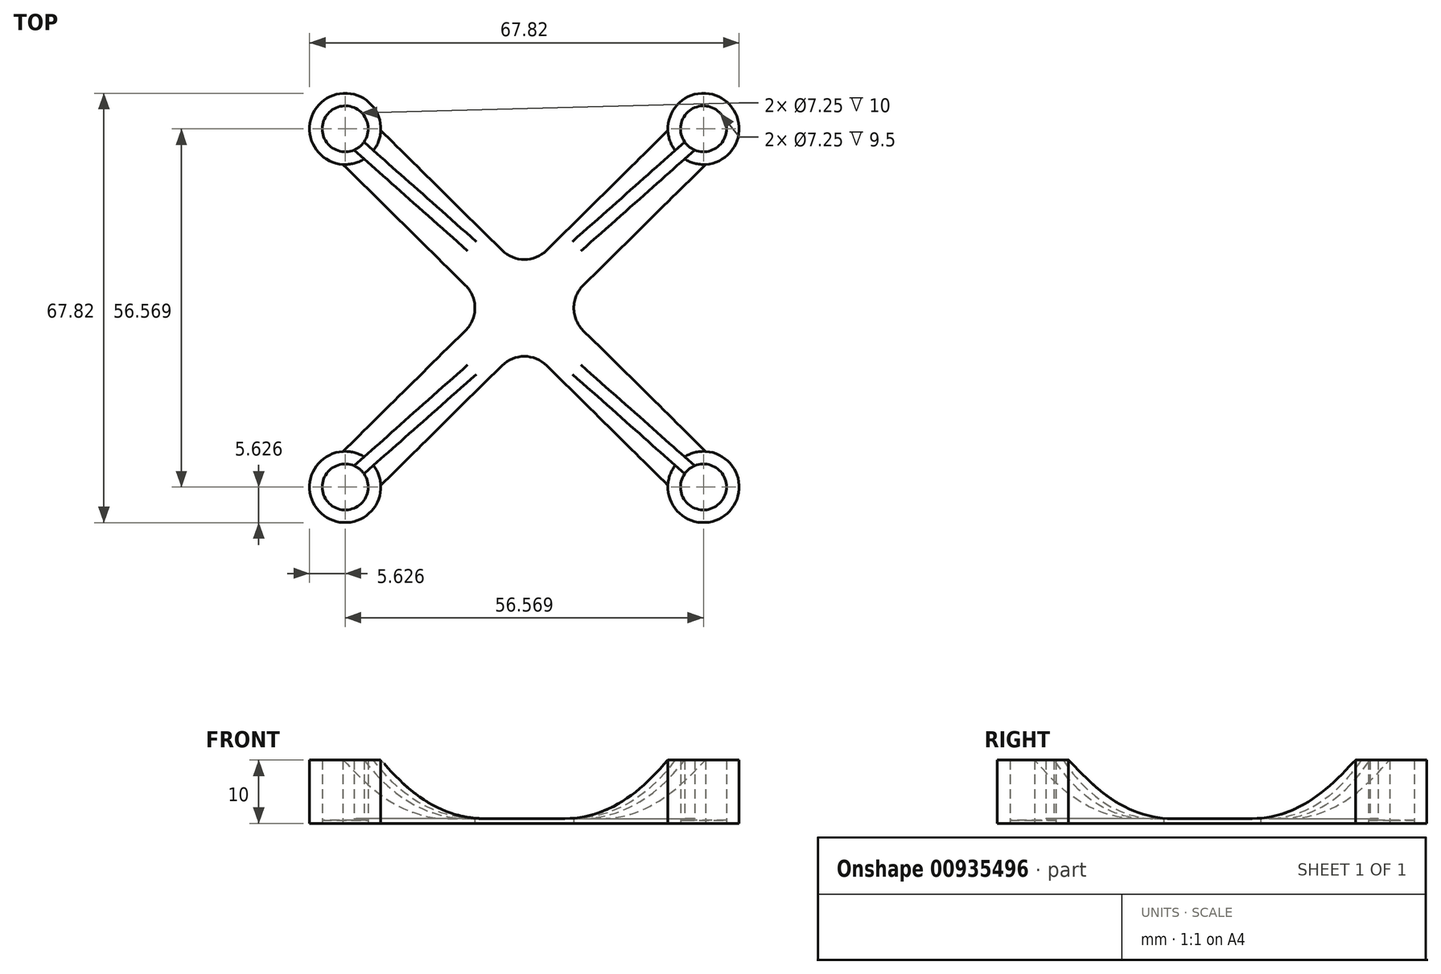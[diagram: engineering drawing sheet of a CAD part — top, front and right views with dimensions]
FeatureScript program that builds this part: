
annotation { "Feature Type Name" : "Feature", "Feature Type Description" : "" }
export const myFeature = defineFeature(function(context is Context, id is Id, definition is map)
    precondition{}
    {
        {
            var Q0;
            Q0=qCreatedBy(makeId("Top.planeOp"),FACE);
            var sketch = newSketch(context, id + "F0", { "sketchPlane" : qUnion([Q0])});
            skLineSegment(sketch, "E0", {"start": v(-28.63, 22.67) * mm, "end": v(22.67, -28.03) * mm});
            skLineSegment(sketch, "E1", {"start": v(28.63, -22.67) * mm, "end": v(-22.67, 28.03) * mm});
            skLineSegment(sketch, "E2.MirrorCS", {"start": v(28.63, 22.67) * mm, "end": v(-22.67, -28.03) * mm});
            skLineSegment(sketch, "E3.MirrorCS", {"start": v(-28.63, -22.67) * mm, "end": v(22.67, 28.03) * mm});
            skPoint(sketch, "E4", {"position": v(0, 5.62) * mm});
            skPoint(sketch, "E5", {"position": v(5.7, 0) * mm});
            skPoint(sketch, "E6", {"position": v(0, -5.62) * mm});
            skPoint(sketch, "E7", {"position": v(-5.7, 0) * mm});
            skPoint(sketch, "E8.middle", {"position": v(0, 0) * mm});
            skCircle(sketch, "E9.MirrorC", {"center": v(-28.28, 28.28) * mm, "radius": 3.62 * mm});
            skCircle(sketch, "E10", {"center": v(-28.28, 28.28) * mm, "radius": 5.62 * mm});
            skCircle(sketch, "E11.MirrorC", {"center": v(28.28, 28.28) * mm, "radius": 3.62 * mm});
            skCircle(sketch, "E12.MirrorC", {"center": v(28.28, 28.28) * mm, "radius": 5.62 * mm});
            skCircle(sketch, "E13.MirrorC", {"center": v(28.28, -28.28) * mm, "radius": 5.62 * mm});
            skCircle(sketch, "E14.MirrorC", {"center": v(28.28, -28.28) * mm, "radius": 3.62 * mm});
            skCircle(sketch, "E15.MirrorC", {"center": v(-28.28, -28.28) * mm, "radius": 5.62 * mm});
            skCircle(sketch, "E16.MirrorC", {"center": v(-28.28, -28.28) * mm, "radius": 3.62 * mm});
            skLineSegment(sketch, "E17", {"start": v(-28.28, 28.28) * mm, "end": v(-28.28, -28.28) * mm, "construction": true});
            skLineSegment(sketch, "E18", {"start": v(28.28, -28.28) * mm, "end": v(28.28, 28.28) * mm, "construction": true});
            skLineSegment(sketch, "E19", {"start": v(28.28, 28.28) * mm, "end": v(-28.28, 28.28) * mm, "construction": true});
            skLineSegment(sketch, "E20", {"start": v(-28.28, -28.28) * mm, "end": v(28.28, -28.28) * mm, "construction": true});
            skLineSegment(sketch, "E21", {"start": v(-25.31, 26.2) * mm, "end": v(-23.81, 24.87) * mm});
            skLineSegment(sketch, "E22", {"start": v(-26.9, 24.94) * mm, "end": v(-25.3, 23.52) * mm});
            skLineSegment(sketch, "E23.MirrorCS", {"start": v(26.9, 24.94) * mm, "end": v(25.3, 23.52) * mm});
            skLineSegment(sketch, "E24.MirrorCS", {"start": v(25.31, 26.2) * mm, "end": v(23.81, 24.87) * mm});
            skLineSegment(sketch, "E25.MirrorCS", {"start": v(26.9, -24.94) * mm, "end": v(25.3, -23.52) * mm});
            skLineSegment(sketch, "E26.MirrorCS", {"start": v(25.31, -26.2) * mm, "end": v(23.81, -24.87) * mm});
            skLineSegment(sketch, "E27.MirrorCS", {"start": v(-26.9, -24.94) * mm, "end": v(-25.3, -23.52) * mm});
            skLineSegment(sketch, "E28.MirrorCS", {"start": v(-25.31, -26.2) * mm, "end": v(-23.81, -24.87) * mm});
            skSolve(sketch);
        }
        {
            var Q0;
            {var subQ0=sQuery(id+"F0.wireOp",EDGE,"E3.MirrorCS");var subQ1=sQuery(id+"F0.wireOp",EDGE,"E0");var subQ2=makeQuery(id+"F0.imprint","INTERSECT",VERTEX,{"derivedFrom":[subQ1,subQ0]});Q0=makeQuery(id+"F0.imprint","IMPRINT",FACE,{"disambiguationData":[TD([[makeQuery(id+"F0.imprint","IMPRINT",EDGE,{"disambiguationData":[TD([[subQ2,-1.0]])],"derivedFrom":subQ1}),-1.0]])]});}
            var Q1;
            {var subQ0=sQuery(id+"F0.wireOp",EDGE,"E10");var subQ1=sQuery(id+"F0.wireOp",EDGE,"E0");var subQ2=makeQuery(id+"F0.imprint","INTERSECT",VERTEX,{"derivedFrom":[subQ1,subQ0]});Q1=makeQuery(id+"F0.imprint","IMPRINT",FACE,{"disambiguationData":[TD([[makeQuery(id+"F0.imprint","IMPRINT",EDGE,{"disambiguationData":[TD([[subQ2,-1.0]])],"derivedFrom":subQ1}),1.0]])]});}
            var Q2;
            {var subQ0=sQuery(id+"F0.wireOp",EDGE,"E2.MirrorCS");var subQ1=sQuery(id+"F0.wireOp",EDGE,"E1");var subQ2=makeQuery(id+"F0.imprint","INTERSECT",VERTEX,{"derivedFrom":[subQ1,subQ0]});Q2=makeQuery(id+"F0.imprint","IMPRINT",FACE,{"disambiguationData":[TD([[makeQuery(id+"F0.imprint","IMPRINT",EDGE,{"disambiguationData":[TD([[subQ2,-1.0]])],"derivedFrom":subQ1}),-1.0]])]});}
            var Q3;
            {var subQ0=sQuery(id+"F0.wireOp",EDGE,"E13.MirrorC");var subQ1=sQuery(id+"F0.wireOp",EDGE,"E0");var subQ2=makeQuery(id+"F0.imprint","INTERSECT",VERTEX,{"derivedFrom":[subQ1,subQ0]});Q3=makeQuery(id+"F0.imprint","IMPRINT",FACE,{"disambiguationData":[TD([[makeQuery(id+"F0.imprint","IMPRINT",EDGE,{"disambiguationData":[TD([[subQ2,1.0]])],"derivedFrom":subQ1}),1.0]])]});}
            var Q4;
            {var subQ0=sQuery(id+"F0.wireOp",EDGE,"E3.MirrorCS");var subQ1=sQuery(id+"F0.wireOp",EDGE,"E0");var subQ2=makeQuery(id+"F0.imprint","INTERSECT",VERTEX,{"derivedFrom":[subQ1,subQ0]});Q4=makeQuery(id+"F0.imprint","IMPRINT",FACE,{"disambiguationData":[TD([[makeQuery(id+"F0.imprint","IMPRINT",EDGE,{"disambiguationData":[TD([[subQ2,-1.0]])],"derivedFrom":subQ1}),1.0]])]});}
            var Q5;
            {var subQ3=sQuery(id+"F0.wireOp",EDGE,"E21");Q5=makeQuery(id+"F0.imprint","IMPRINT",FACE,{"disambiguationData":[TD([[makeQuery(id+"F0.imprint","IMPRINT",EDGE,{"derivedFrom":subQ3}),1.0]])]});}
            var Q6;
            {var subQ4=sQuery(id+"F0.wireOp",EDGE,"E23.MirrorCS");Q6=makeQuery(id+"F0.imprint","IMPRINT",FACE,{"disambiguationData":[TD([[makeQuery(id+"F0.imprint","IMPRINT",EDGE,{"derivedFrom":subQ4}),1.0]])]});}
            var Q7;
            {var subQ4=sQuery(id+"F0.wireOp",EDGE,"E25.MirrorCS");Q7=makeQuery(id+"F0.imprint","IMPRINT",FACE,{"disambiguationData":[TD([[makeQuery(id+"F0.imprint","IMPRINT",EDGE,{"derivedFrom":subQ4}),-1.0]])]});}
            var Q8;
            {var subQ4=sQuery(id+"F0.wireOp",EDGE,"E27.MirrorCS");Q8=makeQuery(id+"F0.imprint","IMPRINT",FACE,{"disambiguationData":[TD([[makeQuery(id+"F0.imprint","IMPRINT",EDGE,{"derivedFrom":subQ4}),1.0]])]});}
            var Q9;
            {var subQ0=sQuery(id+"F0.wireOp",EDGE,"E23.MirrorCS");Q9=makeQuery(id+"F0.imprint","IMPRINT",FACE,{"disambiguationData":[TD([[makeQuery(id+"F0.imprint","IMPRINT",EDGE,{"derivedFrom":subQ0}),-1.0]])]});}
            var Q10;
            {var subQ0=sQuery(id+"F0.wireOp",EDGE,"E21");Q10=makeQuery(id+"F0.imprint","IMPRINT",FACE,{"disambiguationData":[TD([[makeQuery(id+"F0.imprint","IMPRINT",EDGE,{"derivedFrom":subQ0}),-1.0]])]});}
            var Q11;
            {var subQ0=sQuery(id+"F0.wireOp",EDGE,"E27.MirrorCS");Q11=makeQuery(id+"F0.imprint","IMPRINT",FACE,{"disambiguationData":[TD([[makeQuery(id+"F0.imprint","IMPRINT",EDGE,{"derivedFrom":subQ0}),-1.0]])]});}
            var Q12;
            {var subQ0=sQuery(id+"F0.wireOp",EDGE,"E25.MirrorCS");Q12=makeQuery(id+"F0.imprint","IMPRINT",FACE,{"disambiguationData":[TD([[makeQuery(id+"F0.imprint","IMPRINT",EDGE,{"derivedFrom":subQ0}),1.0]])]});}
            extrude(context, id + "F1", {"entities" : qUnion([Q0, Q1, Q2, Q3, Q4, Q5, Q6, Q7, Q8, Q9, Q10, Q11, Q12]), "depth" : 0.75 * mm, "offsetDistance" : 25 * mm});
        }
        {
            var Q0;
            {var subQ4=sQuery(id+"F0.wireOp",EDGE,"E27.MirrorCS");Q0=makeQuery(id+"F0.imprint","IMPRINT",FACE,{"disambiguationData":[TD([[makeQuery(id+"F0.imprint","IMPRINT",EDGE,{"derivedFrom":subQ4}),1.0]])]});}
            var Q1;
            {var subQ4=sQuery(id+"F0.wireOp",EDGE,"E25.MirrorCS");Q1=makeQuery(id+"F0.imprint","IMPRINT",FACE,{"disambiguationData":[TD([[makeQuery(id+"F0.imprint","IMPRINT",EDGE,{"derivedFrom":subQ4}),-1.0]])]});}
            var Q2;
            {var subQ4=sQuery(id+"F0.wireOp",EDGE,"E23.MirrorCS");Q2=makeQuery(id+"F0.imprint","IMPRINT",FACE,{"disambiguationData":[TD([[makeQuery(id+"F0.imprint","IMPRINT",EDGE,{"derivedFrom":subQ4}),1.0]])]});}
            var Q3;
            {var subQ3=sQuery(id+"F0.wireOp",EDGE,"E21");Q3=makeQuery(id+"F0.imprint","IMPRINT",FACE,{"disambiguationData":[TD([[makeQuery(id+"F0.imprint","IMPRINT",EDGE,{"derivedFrom":subQ3}),1.0]])]});}
            extrude(context, id + "F2", {"entities" : qUnion([Q0, Q1, Q2, Q3]), "operationType" : NewBodyOperationType.ADD, "depth" : 10 * mm, "offsetDistance" : 25 * mm});
        }
        {
            var Q0;
            Q0=makeQuery(id+"F1.opExtrude","SWEPT_EDGE",EDGE,{"disambiguationData":[OSD([sQuery(id+"F0.wireOp",EDGE,"E1"),sQuery(id+"F0.wireOp",EDGE,"E2.MirrorCS")])]});
            var Q1;
            Q1=makeQuery(id+"F1.opExtrude","SWEPT_EDGE",EDGE,{"disambiguationData":[OSD([sQuery(id+"F0.wireOp",EDGE,"E1"),sQuery(id+"F0.wireOp",EDGE,"E3.MirrorCS")])]});
            var Q2;
            Q2=makeQuery(id+"F1.opExtrude","SWEPT_EDGE",EDGE,{"disambiguationData":[OSD([sQuery(id+"F0.wireOp",EDGE,"E0"),sQuery(id+"F0.wireOp",EDGE,"E3.MirrorCS")])]});
            var Q3;
            Q3=makeQuery(id+"F1.opExtrude","SWEPT_EDGE",EDGE,{"disambiguationData":[OSD([sQuery(id+"F0.wireOp",EDGE,"E0"),sQuery(id+"F0.wireOp",EDGE,"E2.MirrorCS")])]});
            fillet(context, id + "F3", {"entities" : qUnion([Q0, Q1, Q2, Q3]), "radius" : 5 * mm, "tangentPropagation" : true, "allowEdgeOverflow" : false});
        }
        {
            var Q0;
            Q0=makeQuery(id+"F0.imprint","IMPRINT",FACE,{"disambiguationData":[TD([[makeQuery(id+"F0.imprint","IMPRINT",EDGE,{"derivedFrom":sQuery(id+"F0.wireOp",EDGE,"E9.MirrorC")}),-1.0]])]});
            var Q1;
            Q1=makeQuery(id+"F0.imprint","IMPRINT",FACE,{"disambiguationData":[TD([[makeQuery(id+"F0.imprint","IMPRINT",EDGE,{"derivedFrom":sQuery(id+"F0.wireOp",EDGE,"E11.MirrorC")}),1.0]])]});
            var Q2;
            Q2=makeQuery(id+"F0.imprint","IMPRINT",FACE,{"disambiguationData":[TD([[makeQuery(id+"F0.imprint","IMPRINT",EDGE,{"derivedFrom":sQuery(id+"F0.wireOp",EDGE,"E14.MirrorC")}),-1.0]])]});
            var Q3;
            Q3=makeQuery(id+"F0.imprint","IMPRINT",FACE,{"disambiguationData":[TD([[makeQuery(id+"F0.imprint","IMPRINT",EDGE,{"derivedFrom":sQuery(id+"F0.wireOp",EDGE,"E16.MirrorC")}),1.0]])]});
            extrude(context, id + "F4", {"entities" : qUnion([Q0, Q1, Q2, Q3]), "operationType" : NewBodyOperationType.ADD, "depth" : .5 * mm, "offsetDistance" : 25 * mm});
        }
        {
            var Q0;
            {var subQ0=sQuery(id+"F0.wireOp",EDGE,"E10");Q0=makeQuery(id+"F2.boolean.opBoolean","INTERSECT",EDGE,{"disambiguationData":[OD(0.0)],"derivedFrom":[makeQuery(id+"F1.opExtrude","CAP_FACE",FACE,{"disambiguationData":[OSD([sQuery(id+"F0.wireOp",EDGE,"E0"),sQuery(id+"F0.wireOp",EDGE,"E1"),sQuery(id+"F0.wireOp",EDGE,"E2.MirrorCS"),sQuery(id+"F0.wireOp",EDGE,"E3.MirrorCS"),sQuery(id+"F0.wireOp",EDGE,"E9.MirrorC"),subQ0,sQuery(id+"F0.wireOp",EDGE,"E11.MirrorC"),sQuery(id+"F0.wireOp",EDGE,"E12.MirrorC"),sQuery(id+"F0.wireOp",EDGE,"E13.MirrorC"),sQuery(id+"F0.wireOp",EDGE,"E14.MirrorC"),sQuery(id+"F0.wireOp",EDGE,"E15.MirrorC"),sQuery(id+"F0.wireOp",EDGE,"E16.MirrorC")])],"isStart":false}),makeQuery(id+"F2.opExtrude","SWEPT_FACE",FACE,{"disambiguationData":[OSD([subQ0])]})]});}
            var Q1;
            {var subQ0=sQuery(id+"F0.wireOp",EDGE,"E10");Q1=makeQuery(id+"F2.boolean.opBoolean","INTERSECT",EDGE,{"disambiguationData":[OD(1.0)],"derivedFrom":[makeQuery(id+"F1.opExtrude","CAP_FACE",FACE,{"disambiguationData":[OSD([sQuery(id+"F0.wireOp",EDGE,"E0"),sQuery(id+"F0.wireOp",EDGE,"E1"),sQuery(id+"F0.wireOp",EDGE,"E2.MirrorCS"),sQuery(id+"F0.wireOp",EDGE,"E3.MirrorCS"),sQuery(id+"F0.wireOp",EDGE,"E9.MirrorC"),subQ0,sQuery(id+"F0.wireOp",EDGE,"E11.MirrorC"),sQuery(id+"F0.wireOp",EDGE,"E12.MirrorC"),sQuery(id+"F0.wireOp",EDGE,"E13.MirrorC"),sQuery(id+"F0.wireOp",EDGE,"E14.MirrorC"),sQuery(id+"F0.wireOp",EDGE,"E15.MirrorC"),sQuery(id+"F0.wireOp",EDGE,"E16.MirrorC")])],"isStart":false}),makeQuery(id+"F2.opExtrude","SWEPT_FACE",FACE,{"disambiguationData":[OSD([subQ0])]})]});}
            var Q2;
            {var subQ0=sQuery(id+"F0.wireOp",EDGE,"E15.MirrorC");Q2=makeQuery(id+"F2.boolean.opBoolean","INTERSECT",EDGE,{"disambiguationData":[OD(0.0)],"derivedFrom":[makeQuery(id+"F1.opExtrude","CAP_FACE",FACE,{"disambiguationData":[OSD([sQuery(id+"F0.wireOp",EDGE,"E0"),sQuery(id+"F0.wireOp",EDGE,"E1"),sQuery(id+"F0.wireOp",EDGE,"E2.MirrorCS"),sQuery(id+"F0.wireOp",EDGE,"E3.MirrorCS"),sQuery(id+"F0.wireOp",EDGE,"E9.MirrorC"),sQuery(id+"F0.wireOp",EDGE,"E10"),sQuery(id+"F0.wireOp",EDGE,"E11.MirrorC"),sQuery(id+"F0.wireOp",EDGE,"E12.MirrorC"),sQuery(id+"F0.wireOp",EDGE,"E13.MirrorC"),sQuery(id+"F0.wireOp",EDGE,"E14.MirrorC"),subQ0,sQuery(id+"F0.wireOp",EDGE,"E16.MirrorC")])],"isStart":false}),makeQuery(id+"F2.opExtrude","SWEPT_FACE",FACE,{"disambiguationData":[OSD([subQ0])]})]});}
            var Q3;
            {var subQ0=sQuery(id+"F0.wireOp",EDGE,"E15.MirrorC");Q3=makeQuery(id+"F2.boolean.opBoolean","INTERSECT",EDGE,{"disambiguationData":[OD(1.0)],"derivedFrom":[makeQuery(id+"F1.opExtrude","CAP_FACE",FACE,{"disambiguationData":[OSD([sQuery(id+"F0.wireOp",EDGE,"E0"),sQuery(id+"F0.wireOp",EDGE,"E1"),sQuery(id+"F0.wireOp",EDGE,"E2.MirrorCS"),sQuery(id+"F0.wireOp",EDGE,"E3.MirrorCS"),sQuery(id+"F0.wireOp",EDGE,"E9.MirrorC"),sQuery(id+"F0.wireOp",EDGE,"E10"),sQuery(id+"F0.wireOp",EDGE,"E11.MirrorC"),sQuery(id+"F0.wireOp",EDGE,"E12.MirrorC"),sQuery(id+"F0.wireOp",EDGE,"E13.MirrorC"),sQuery(id+"F0.wireOp",EDGE,"E14.MirrorC"),subQ0,sQuery(id+"F0.wireOp",EDGE,"E16.MirrorC")])],"isStart":false}),makeQuery(id+"F2.opExtrude","SWEPT_FACE",FACE,{"disambiguationData":[OSD([subQ0])]})]});}
            var Q4;
            {var subQ0=sQuery(id+"F0.wireOp",EDGE,"E12.MirrorC");Q4=makeQuery(id+"F2.boolean.opBoolean","INTERSECT",EDGE,{"disambiguationData":[OD(0.0)],"derivedFrom":[makeQuery(id+"F1.opExtrude","CAP_FACE",FACE,{"disambiguationData":[OSD([sQuery(id+"F0.wireOp",EDGE,"E0"),sQuery(id+"F0.wireOp",EDGE,"E1"),sQuery(id+"F0.wireOp",EDGE,"E2.MirrorCS"),sQuery(id+"F0.wireOp",EDGE,"E3.MirrorCS"),sQuery(id+"F0.wireOp",EDGE,"E9.MirrorC"),sQuery(id+"F0.wireOp",EDGE,"E10"),sQuery(id+"F0.wireOp",EDGE,"E11.MirrorC"),subQ0,sQuery(id+"F0.wireOp",EDGE,"E13.MirrorC"),sQuery(id+"F0.wireOp",EDGE,"E14.MirrorC"),sQuery(id+"F0.wireOp",EDGE,"E15.MirrorC"),sQuery(id+"F0.wireOp",EDGE,"E16.MirrorC")])],"isStart":false}),makeQuery(id+"F2.opExtrude","SWEPT_FACE",FACE,{"disambiguationData":[OSD([subQ0])]})]});}
            var Q5;
            {var subQ0=sQuery(id+"F0.wireOp",EDGE,"E12.MirrorC");Q5=makeQuery(id+"F2.boolean.opBoolean","INTERSECT",EDGE,{"disambiguationData":[OD(1.0)],"derivedFrom":[makeQuery(id+"F1.opExtrude","CAP_FACE",FACE,{"disambiguationData":[OSD([sQuery(id+"F0.wireOp",EDGE,"E0"),sQuery(id+"F0.wireOp",EDGE,"E1"),sQuery(id+"F0.wireOp",EDGE,"E2.MirrorCS"),sQuery(id+"F0.wireOp",EDGE,"E3.MirrorCS"),sQuery(id+"F0.wireOp",EDGE,"E9.MirrorC"),sQuery(id+"F0.wireOp",EDGE,"E10"),sQuery(id+"F0.wireOp",EDGE,"E11.MirrorC"),subQ0,sQuery(id+"F0.wireOp",EDGE,"E13.MirrorC"),sQuery(id+"F0.wireOp",EDGE,"E14.MirrorC"),sQuery(id+"F0.wireOp",EDGE,"E15.MirrorC"),sQuery(id+"F0.wireOp",EDGE,"E16.MirrorC")])],"isStart":false}),makeQuery(id+"F2.opExtrude","SWEPT_FACE",FACE,{"disambiguationData":[OSD([subQ0])]})]});}
            var Q6;
            {var subQ0=sQuery(id+"F0.wireOp",EDGE,"E13.MirrorC");Q6=makeQuery(id+"F2.boolean.opBoolean","INTERSECT",EDGE,{"disambiguationData":[OD(0.0)],"derivedFrom":[makeQuery(id+"F1.opExtrude","CAP_FACE",FACE,{"disambiguationData":[OSD([sQuery(id+"F0.wireOp",EDGE,"E0"),sQuery(id+"F0.wireOp",EDGE,"E1"),sQuery(id+"F0.wireOp",EDGE,"E2.MirrorCS"),sQuery(id+"F0.wireOp",EDGE,"E3.MirrorCS"),sQuery(id+"F0.wireOp",EDGE,"E9.MirrorC"),sQuery(id+"F0.wireOp",EDGE,"E10"),sQuery(id+"F0.wireOp",EDGE,"E11.MirrorC"),sQuery(id+"F0.wireOp",EDGE,"E12.MirrorC"),subQ0,sQuery(id+"F0.wireOp",EDGE,"E14.MirrorC"),sQuery(id+"F0.wireOp",EDGE,"E15.MirrorC"),sQuery(id+"F0.wireOp",EDGE,"E16.MirrorC")])],"isStart":false}),makeQuery(id+"F2.opExtrude","SWEPT_FACE",FACE,{"disambiguationData":[OSD([subQ0])]})]});}
            var Q7;
            {var subQ0=sQuery(id+"F0.wireOp",EDGE,"E13.MirrorC");Q7=makeQuery(id+"F2.boolean.opBoolean","INTERSECT",EDGE,{"disambiguationData":[OD(1.0)],"derivedFrom":[makeQuery(id+"F1.opExtrude","CAP_FACE",FACE,{"disambiguationData":[OSD([sQuery(id+"F0.wireOp",EDGE,"E0"),sQuery(id+"F0.wireOp",EDGE,"E1"),sQuery(id+"F0.wireOp",EDGE,"E2.MirrorCS"),sQuery(id+"F0.wireOp",EDGE,"E3.MirrorCS"),sQuery(id+"F0.wireOp",EDGE,"E9.MirrorC"),sQuery(id+"F0.wireOp",EDGE,"E10"),sQuery(id+"F0.wireOp",EDGE,"E11.MirrorC"),sQuery(id+"F0.wireOp",EDGE,"E12.MirrorC"),subQ0,sQuery(id+"F0.wireOp",EDGE,"E14.MirrorC"),sQuery(id+"F0.wireOp",EDGE,"E15.MirrorC"),sQuery(id+"F0.wireOp",EDGE,"E16.MirrorC")])],"isStart":false}),makeQuery(id+"F2.opExtrude","SWEPT_FACE",FACE,{"disambiguationData":[OSD([subQ0])]})]});}
            fillet(context, id + "F5", {"entities" : qUnion([Q0, Q1, Q2, Q3, Q4, Q5, Q6, Q7]), "radius" : 30 * mm, "tangentPropagation" : true, "allowEdgeOverflow" : false});
        }
    });
